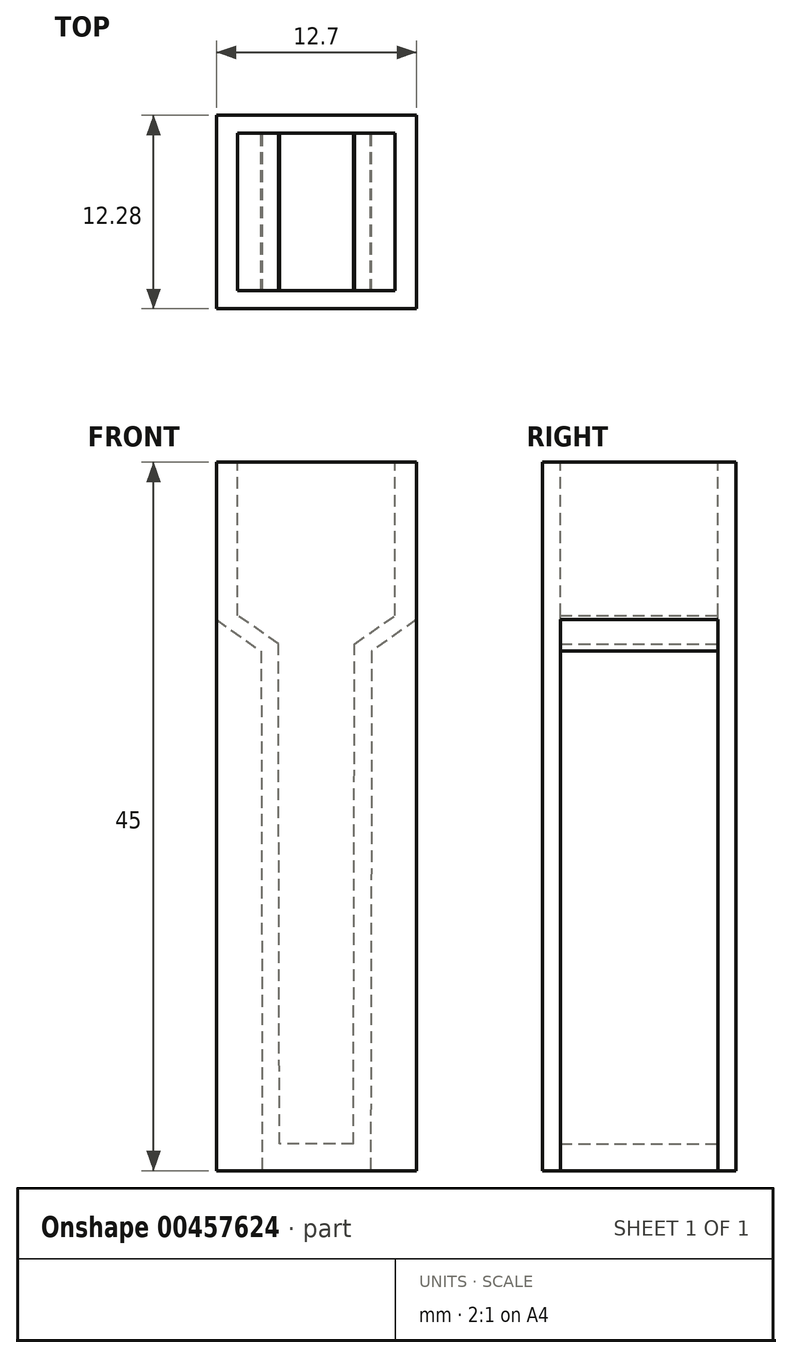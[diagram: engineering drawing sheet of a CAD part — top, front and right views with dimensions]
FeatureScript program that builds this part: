
annotation { "Feature Type Name" : "Feature", "Feature Type Description" : "" }
export const myFeature = defineFeature(function(context is Context, id is Id, definition is map)
    precondition{}
    {
        {
            var Q0;
            Q0=qCreatedBy(makeId("Front.planeOp"),FACE);
            var sketch = newSketch(context, id + "F0", { "sketchPlane" : qUnion([Q0])});
            skLineSegment(sketch, "E0", {"start": v(-6.35, 45) * mm, "end": v(-6.35, 35) * mm});
            skLineSegment(sketch, "E1", {"start": v(-6.35, 35) * mm, "end": v(-3.51, 33) * mm});
            skLineSegment(sketch, "E2", {"start": v(-3.51, 33) * mm, "end": v(-3.44, 0) * mm});
            skLineSegment(sketch, "E3", {"start": v(-3.44, 0) * mm, "end": v(0, 0) * mm});
            skLineSegment(sketch, "E4", {"start": v(0, 0) * mm, "end": v(0, 1.69) * mm});
            skLineSegment(sketch, "E5", {"start": v(0, 1.69) * mm, "end": v(-2.35, 1.69) * mm});
            skLineSegment(sketch, "E6", {"start": v(-2.35, 1.69) * mm, "end": v(-2.42, 33.45) * mm});
            skLineSegment(sketch, "E7", {"start": v(-2.42, 33.45) * mm, "end": v(-5, 35.27) * mm});
            skLineSegment(sketch, "E8", {"start": v(-5, 35.27) * mm, "end": v(-5, 45) * mm});
            skLineSegment(sketch, "E9", {"start": v(-5, 45) * mm, "end": v(-6.35, 45) * mm});
            skLineSegment(sketch, "E10.MirrorCS", {"start": v(6.35, 35) * mm, "end": v(3.51, 33) * mm});
            skLineSegment(sketch, "E11.MirrorCS", {"start": v(0, 1.69) * mm, "end": v(2.35, 1.69) * mm});
            skLineSegment(sketch, "E12.MirrorCS", {"start": v(2.42, 33.45) * mm, "end": v(5, 35.27) * mm});
            skLineSegment(sketch, "E13.MirrorCS", {"start": v(5, 45) * mm, "end": v(6.35, 45) * mm});
            skLineSegment(sketch, "E14.MirrorCS", {"start": v(3.51, 33) * mm, "end": v(3.44, 0) * mm});
            skLineSegment(sketch, "E15.MirrorCS", {"start": v(3.44, 0) * mm, "end": v(0, 0) * mm});
            skLineSegment(sketch, "E16.MirrorCS", {"start": v(2.35, 1.69) * mm, "end": v(2.42, 33.45) * mm});
            skLineSegment(sketch, "E17.MirrorCS", {"start": v(5, 35.27) * mm, "end": v(5, 45) * mm});
            skLineSegment(sketch, "E18.MirrorCS", {"start": v(6.35, 45) * mm, "end": v(6.35, 35) * mm});
            skSolve(sketch);
        }
        {
            var Q0;
            Q0=makeQuery(id+"F0.imprint","IMPRINT",FACE,{"disambiguationData":[TD([[makeQuery(id+"F0.imprint","IMPRINT",EDGE,{"derivedFrom":sQuery(id+"F0.wireOp",EDGE,"E0")}),1.0]])]});
            var Q1;
            Q1=makeQuery(id+"F0.imprint","IMPRINT",FACE,{"disambiguationData":[TD([[makeQuery(id+"F0.imprint","IMPRINT",EDGE,{"derivedFrom":sQuery(id+"F0.wireOp",EDGE,"E10.MirrorCS")}),-1.0]])]});
            extrude(context, id + "F1", {"entities" : qUnion([Q0, Q1]), "depth" : 10 * mm, "offsetDistance" : 25 * mm});
        }
        {
            var Q0;
            Q0=qCreatedBy(makeId("Front.planeOp"),FACE);
            var sketch = newSketch(context, id + "F2", { "sketchPlane" : qUnion([Q0])});
            skLineSegment(sketch, "E19.bottom", {"start": v(6.35, 45) * mm, "end": v(-6.35, 45) * mm});
            skLineSegment(sketch, "E19.top", {"start": v(6.35, 0) * mm, "end": v(-6.35, 0) * mm});
            skLineSegment(sketch, "E19.left", {"start": v(6.35, 45) * mm, "end": v(6.35, 0) * mm});
            skLineSegment(sketch, "E19.right", {"start": v(-6.35, 45) * mm, "end": v(-6.35, 0) * mm});
            skSolve(sketch);
        }
        {
            var Q0;
            Q0 = qSketchRegion(id + "F2", true);
            extrude(context, id + "F3", {"entities" : qUnion([Q0]), "operationType" : NewBodyOperationType.ADD, "oppositeDirection" : true, "depth" : 1.14 * mm});
        }
        {
            var Q0;
            Q0=makeQuery(id+"F1.opExtrude","CAP_FACE",FACE,{"disambiguationData":[OSD([sQuery(id+"F0.wireOp",EDGE,"E0"),sQuery(id+"F0.wireOp",EDGE,"E1"),sQuery(id+"F0.wireOp",EDGE,"E2"),sQuery(id+"F0.wireOp",EDGE,"E3"),sQuery(id+"F0.wireOp",EDGE,"E5"),sQuery(id+"F0.wireOp",EDGE,"E6"),sQuery(id+"F0.wireOp",EDGE,"E7"),sQuery(id+"F0.wireOp",EDGE,"E8"),sQuery(id+"F0.wireOp",EDGE,"E9"),sQuery(id+"F0.wireOp",EDGE,"E10.MirrorCS"),sQuery(id+"F0.wireOp",EDGE,"E11.MirrorCS"),sQuery(id+"F0.wireOp",EDGE,"E12.MirrorCS"),sQuery(id+"F0.wireOp",EDGE,"E13.MirrorCS"),sQuery(id+"F0.wireOp",EDGE,"E14.MirrorCS"),sQuery(id+"F0.wireOp",EDGE,"E15.MirrorCS"),sQuery(id+"F0.wireOp",EDGE,"E16.MirrorCS"),sQuery(id+"F0.wireOp",EDGE,"E17.MirrorCS"),sQuery(id+"F0.wireOp",EDGE,"E18.MirrorCS")])],"isStart":false});
            var sketch = newSketch(context, id + "F4", { "sketchPlane" : qUnion([Q0])});
            skLineSegment(sketch, "E20.bottom", {"start": v(-6.35, 45) * mm, "end": v(6.35, 45) * mm});
            skLineSegment(sketch, "E20.top", {"start": v(-6.35, 0) * mm, "end": v(6.35, 0) * mm});
            skLineSegment(sketch, "E20.left", {"start": v(-6.35, 45) * mm, "end": v(-6.35, 0) * mm});
            skLineSegment(sketch, "E20.right", {"start": v(6.35, 45) * mm, "end": v(6.35, 0) * mm});
            skSolve(sketch);
        }
        {
            var Q0;
            Q0 = qSketchRegion(id + "F4", true);
            extrude(context, id + "F5", {"entities" : qUnion([Q0]), "operationType" : NewBodyOperationType.ADD, "depth" : 1.14 * mm});
        }
    });
